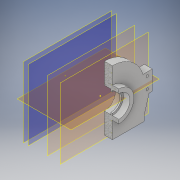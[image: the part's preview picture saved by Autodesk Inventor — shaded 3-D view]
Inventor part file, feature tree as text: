
AUTODESK INVENTOR PART (.ipt)
format: ipt  version: 2019 (Build 230136000, 136)  size: 526,336 bytes
history: native  units: mm
features: sketch x28, extrude x21, mirror x13, plane x12, projected_geometry x11, fillet x4, hole x3, other x2
ambient origin geometry x8: Origin, YZ Plane, XZ Plane, XY Plane, X Axis, Y Axis, Z Axis, Center Point
bodies: Body1 (feature_tree)
feature tree (94):
  other  "實體1"
  extrude  "擠出1"  Depth=123.43mm
  plane  "工作平面2"
  extrude  "擠出3"  Depth=160.0mm
  plane  "工作平面3"
  sketch  "草圖5"
  extrude  "擠出4"  Depth=120.0mm TaperAngle=0.0deg
  extrude  "擠出5"  [1 undecoded]
  plane  "工作平面4"
  extrude  "擠出7"  Depth=130.0mm
  plane  "工作平面5"
  extrude  "擠出9"  Depth=15.0mm TaperAngle=0.0deg
  extrude  "擠出10"  [1 undecoded]
  extrude  "擠出11"  Depth=140.0mm
  extrude  "擠出12"  Depth=10.0mm TaperAngle=0.0deg
  mirror  "鏡射1"
  fillet  "圓角2"  Radius=10.0mm
  fillet  "圓角3"  Radius=10.0mm
  sketch  "草圖16"
  plane  "工作平面7"
  mirror  "鏡射2"
  fillet  "圓角5"  [1 undecoded]
  fillet  "圓角6"  Radius=10.0mm
  plane  "工作平面8"
  plane  "工作平面9"
  sketch  "草圖20"
  sketch  "草圖21"
  extrude  "擠出15"  [1 undecoded]
  plane  "工作平面10"
  extrude  "擠出16"  Depth=10.0mm
  extrude  "擠出17"  Depth=10.0mm TaperAngle=0.0deg
  plane  "工作平面11"
  extrude  "擠出19"  Depth=10.0mm TaperAngle=0.0deg
  extrude  "擠出20"  Depth=160.0mm
  mirror  "鏡射3"
  mirror  "鏡射4"
  extrude  "擠出21"  Depth=80.0mm
  mirror  "鏡射7"
  plane  "工作平面15"
  mirror  "鏡射9"
  hole  "孔2"  [1 undecoded]
  mirror  "鏡射10"
  mirror  "鏡射11"
  hole  "孔3"  [1 undecoded]
  mirror  "鏡射12"
  mirror  "鏡射13"
  extrude  "擠出22"  Depth=160.0mm
  extrude  "擠出23"  Depth=120.0mm TaperAngle=0.0deg
  extrude  "擠出24"  Depth=120.0mm TaperAngle=0.0deg
  extrude  "擠出25"  Depth=25.0mm
  extrude  "擠出27"  Depth=20.0mm
  extrude  "擠出28"  Depth=2.0mm
  mirror  "鏡射14"
  plane  "工作平面17"
  hole  "孔4"  [1 undecoded]
  mirror  "鏡射15"
  mirror  "鏡射16"
  other  "分割1"
  sketch  "草圖1"
  sketch  "草圖4"
  sketch  "草圖6"
  sketch  "草圖7"
  projected_geometry  "投影迴路1"
  sketch  "草圖9"
  projected_geometry  "投影迴路4"
  sketch  "草圖11"
  sketch  "草圖12"
  projected_geometry  "投影迴路6"
  sketch  "草圖13"
  projected_geometry  "投影迴路7"
  sketch  "草圖14"
  plane  "工作平面6"
  sketch  "草圖17"
  projected_geometry  "投影迴路8"
  sketch  "草圖24"
  projected_geometry  "投影迴路11"
  sketch  "草圖25"
  sketch  "草圖26"
  sketch  "草圖27"
  sketch  "草圖28"
  sketch  "草圖29"
  projected_geometry  "投影迴路12"
  sketch  "草圖30"
  sketch  "草圖31"
  sketch  "草圖32"
  projected_geometry  "投影迴路13"
  projected_geometry  "投影迴路14"
  projected_geometry  "投影迴路15"
  sketch  "草圖33"
  sketch  "草圖34"
  sketch  "草圖35"
  projected_geometry  "投影迴路16"
  sketch  "草圖36"
  sketch  "草圖37"
note: 7 required parameter values undecoded (feature->parameter linkage not recoverable at this tier; creation-order binding heuristic only, values carry confidence <= 0.55)
